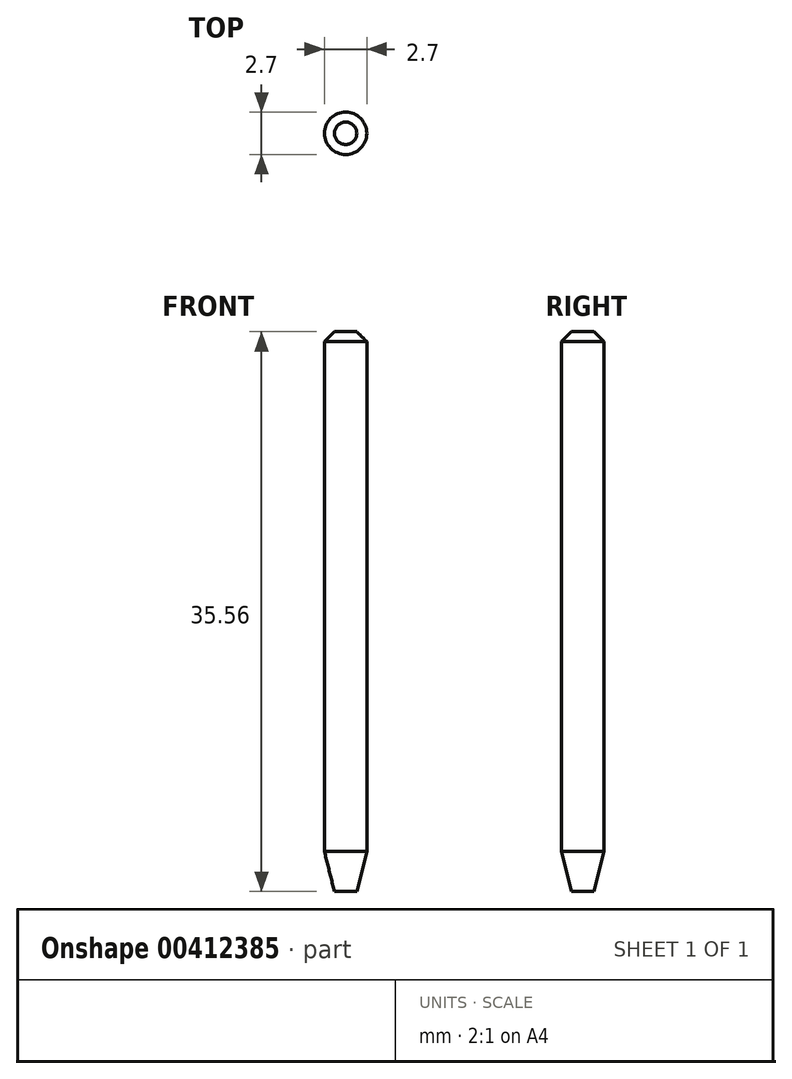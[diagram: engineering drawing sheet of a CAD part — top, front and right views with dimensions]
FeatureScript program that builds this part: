
annotation { "Feature Type Name" : "Feature", "Feature Type Description" : "" }
export const myFeature = defineFeature(function(context is Context, id is Id, definition is map)
    precondition{}
    {
        {
            var Q0;
            Q0=qCreatedBy(makeId("Front.planeOp"),FACE);
            var sketch = newSketch(context, id + "F0", { "sketchPlane" : qUnion([Q0])});
            skLineSegment(sketch, "E0", {"start": v(0, 0) * mm, "end": v(0, 35.56) * mm});
            skLineSegment(sketch, "E1", {"start": v(0, 0) * mm, "end": v(-1.35, 0) * mm});
            skLineSegment(sketch, "E2", {"start": v(-1.35, 35.56) * mm, "end": v(0, 35.56) * mm});
            skLineSegment(sketch, "E3.0", {"start": v(-1.35, 0) * mm, "end": v(-1.35, 12.7) * mm});
            skLineSegment(sketch, "E4.0", {"start": v(-1.35, 12.7) * mm, "end": v(-1.35, 35.56) * mm});
            skLineSegment(sketch, "E5.0", {"start": v(-1.35, 12.7) * mm, "end": v(-1.35, 12.7) * mm});
            skSolve(sketch);
        }
        {
            var Q0;
            Q0=makeQuery(id+"F0.imprint","IMPRINT",FACE,{"disambiguationData":[TD([[makeQuery(id+"F0.imprint","IMPRINT",EDGE,{"derivedFrom":sQuery(id+"F0.wireOp",EDGE,"E0")}),1.0]])]});
            var Q1;
            Q1=sQuery(id+"F0.wireOp",EDGE,"E0");
            revolve(context, id + "F1", {"entities" : qUnion([Q0]), "axis" : qUnion([Q1]), "revolveType" : RevolveType.FULL});
        }
        {
            var Q0;
            Q0=makeQuery(id+"F1.opRevolve","SWEPT_EDGE",EDGE,{"disambiguationData":[OSD([sQuery(id+"F0.wireOp",EDGE,"E1"),sQuery(id+"F0.wireOp",EDGE,"E3.0")])]});
            chamfer(context, id + "F2", {"entities" : qUnion([Q0]), "chamferType" : ChamferType.TWO_OFFSETS, "width1" : 0.64 * mm, "oppositeDirection" : false, "width2" : 2.54 * mm, "tangentPropagation" : true});
        }
        {
            var Q0;
            Q0=makeQuery(id+"F1.opRevolve","SWEPT_EDGE",EDGE,{"disambiguationData":[OSD([sQuery(id+"F0.wireOp",EDGE,"E2"),sQuery(id+"F0.wireOp",EDGE,"E4.0")])]});
            chamfer(context, id + "F3", {"entities" : qUnion([Q0]), "width" : 0.64 * mm, "tangentPropagation" : true});
        }
    });
